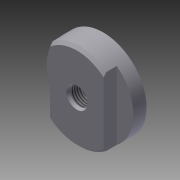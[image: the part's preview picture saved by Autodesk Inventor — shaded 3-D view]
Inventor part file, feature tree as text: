
AUTODESK INVENTOR PART (.ipt)
format: ipt  version: 2014 SP1 (Build 180222100, 222)  size: 108,544 bytes
history: native  units: in
note: dims shown in document units (in); Inventor stores cm internally (conversion verified against a paired STEP export)
features: extrude x2, sketch x2, hole x1, chamfer x1
ambient origin geometry x8: Origin, YZ Plane, XZ Plane, XY Plane, X Axis, Y Axis, Z Axis, Center Point
bodies: Solid1 (feature_tree)
feature tree (6):
  extrude  "Extrusion1"  Depth=0.312in TaperAngle=0.0deg
  extrude  "Extrusion2"  Depth=0.312in TaperAngle=0.0deg
  hole  "Hole1"  [1 undecoded]
  chamfer  "Chamfer1"  Distance=0.0625in Angle=45.0deg
  sketch  "Sketch1"  dims[d0=2.062in d1=0.312in d2=0.0in]
  sketch  "Sketch2"  dims[d5=1.272in d6=0.312in d7=0.0in d8=1.0in d9=1.0in d10=0.422in d11=0.395in d12=0.0246in d13=0.423in d14=0.5in d15=0.25in d16=45.0deg d17=0.75in d18=0.8108in d19=0.0625in d20=0.125in d21=45.0deg]
note: 1 required parameter value undecoded (feature->parameter linkage not recoverable at this tier; creation-order binding heuristic only, values carry confidence <= 0.55)
